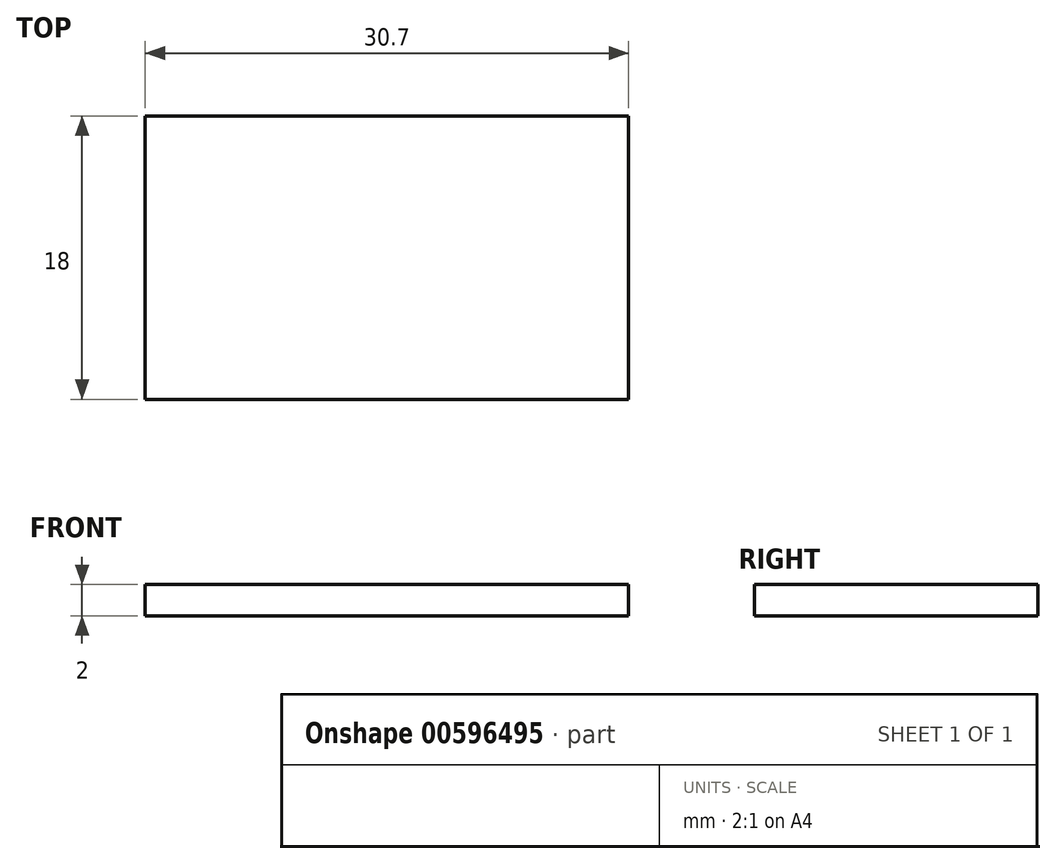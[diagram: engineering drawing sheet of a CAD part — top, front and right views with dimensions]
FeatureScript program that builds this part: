
annotation { "Feature Type Name" : "Feature", "Feature Type Description" : "" }
export const myFeature = defineFeature(function(context is Context, id is Id, definition is map)
    precondition{}
    {
        {
            var Q0;
            Q0=qCreatedBy(makeId("Top.planeOp"),FACE);
            var sketch = newSketch(context, id + "F0", { "sketchPlane" : qUnion([Q0])});
            skLineSegment(sketch, "E0.bottom", {"start": v(-15.35, 9) * mm, "end": v(15.35, 9) * mm});
            skLineSegment(sketch, "E0.top", {"start": v(-15.35, -9) * mm, "end": v(15.35, -9) * mm});
            skLineSegment(sketch, "E0.left", {"start": v(-15.35, 9) * mm, "end": v(-15.35, -9) * mm});
            skLineSegment(sketch, "E0.right", {"start": v(15.35, 9) * mm, "end": v(15.35, -9) * mm});
            skPoint(sketch, "E0.middle", {"position": v(0, 0) * mm});
            skSolve(sketch);
        }
        {
            var Q0;
            Q0=makeQuery(id+"F0.imprint","IMPRINT",FACE,{"disambiguationData":[TD([[makeQuery(id+"F0.imprint","IMPRINT",EDGE,{"derivedFrom":sQuery(id+"F0.wireOp",EDGE,"E0.bottom")}),-1.0]])]});
            extrude(context, id + "F1", {"entities" : qUnion([Q0]), "depth" : 2 * mm, "offsetDistance" : 25 * mm});
        }
    });
